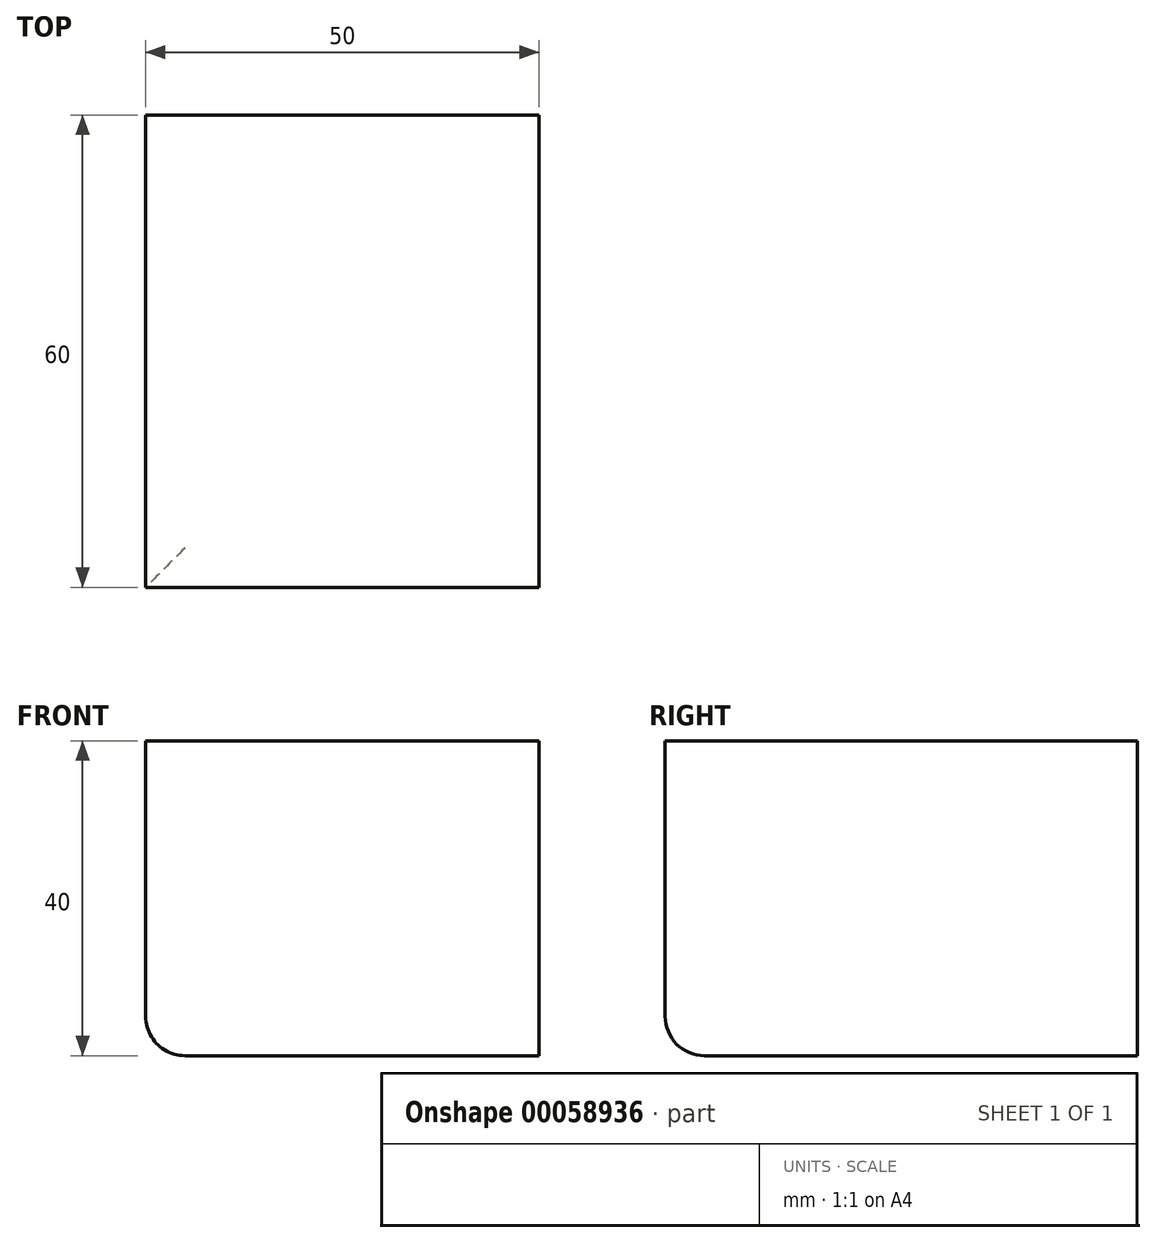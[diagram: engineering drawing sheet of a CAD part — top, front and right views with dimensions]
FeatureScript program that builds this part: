
annotation { "Feature Type Name" : "Feature", "Feature Type Description" : "" }
export const myFeature = defineFeature(function(context is Context, id is Id, definition is map)
    precondition{}
    {
        {
            var Q0;
            Q0=qCreatedBy(makeId("Front.planeOp"),FACE);
            var sketch = newSketch(context, id + "F0", { "sketchPlane" : qUnion([Q0])});
            skLineSegment(sketch, "E0", {"start": v(0, 0) * mm, "end": v(0, 40) * mm});
            skLineSegment(sketch, "E1", {"start": v(0, 40) * mm, "end": v(50, 40) * mm});
            skLineSegment(sketch, "E2", {"start": v(50, 40) * mm, "end": v(50, 0) * mm});
            skLineSegment(sketch, "E3", {"start": v(50, 0) * mm, "end": v(0, 0) * mm});
            skSolve(sketch);
        }
        {
            var Q0;
            Q0 = qSketchRegion(id + "F0", true);
            extrude(context, id + "F1", {"entities" : qUnion([Q0]), "depth" : 60 * mm});
        }
        {
            var Q0;
            Q0=makeQuery(id+"F1.opExtrude","CAP_EDGE",EDGE,{"disambiguationData":[OSD([sQuery(id+"F0.wireOp",EDGE,"E3")])],"isStart":false});
            var Q1;
            Q1=makeQuery(id+"F1.opExtrude","SWEPT_EDGE",EDGE,{"disambiguationData":[OSD([sQuery(id+"F0.wireOp",EDGE,"E0"),sQuery(id+"F0.wireOp",EDGE,"E3")])]});
            fillet(context, id + "F2", {"entities" : qUnion([Q0, Q1]), "radius" : 5 * mm, "tangentPropagation" : true, "allowEdgeOverflow" : false});
        }
    });
